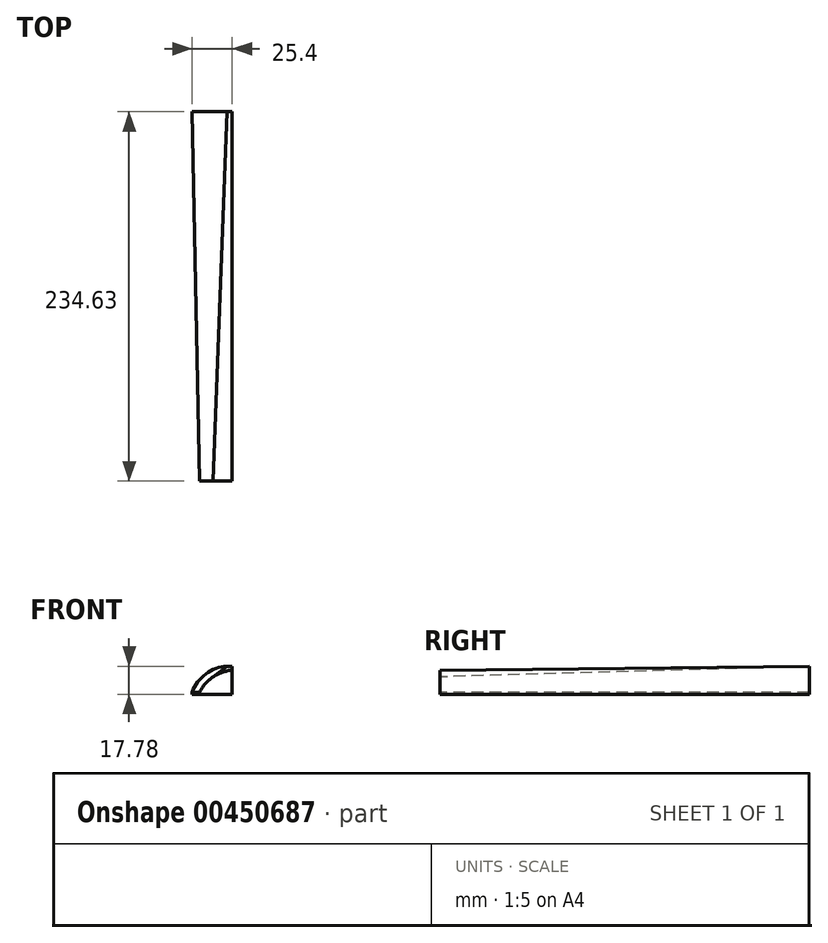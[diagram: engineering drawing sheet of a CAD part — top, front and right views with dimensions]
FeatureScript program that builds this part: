
annotation { "Feature Type Name" : "Feature", "Feature Type Description" : "" }
export const myFeature = defineFeature(function(context is Context, id is Id, definition is map)
    precondition{}
    {
        {
            var Q0;
            Q0=qCreatedBy(makeId("Front.planeOp"),FACE);
            var sketch = newSketch(context, id + "F0", { "sketchPlane" : qUnion([Q0])});
            skLineSegment(sketch, "E0", {"start": v(0, 0) * mm, "end": v(-20.64, 0) * mm});
            skLineSegment(sketch, "E1", {"start": v(0, 0) * mm, "end": v(0, 15.24) * mm});
            skLineSegment(sketch, "E2", {"start": v(-20.64, 0) * mm, "end": v(-20.64, 1.27) * mm});
            skArc(sketch, "E3", {"start": v(0, 15.24) * mm, "mid": v(-12.15, 10.96) * mm, "end": v(-20.64, 1.27) * mm});
            skSolve(sketch);
        }
        {
            var Q0;
            Q0=qCreatedBy(makeId("Right.planeOp"),FACE);
            var sketch = newSketch(context, id + "F1", { "sketchPlane" : qUnion([Q0])});
            skLineSegment(sketch, "E4", {"start": v(234.63, 0) * mm, "end": v(234.63, 17.78) * mm});
            skLineSegment(sketch, "E5", {"start": v(0, 15.24) * mm, "end": v(0, 0) * mm});
            skSolve(sketch);
        }
        {
            var Q0;
            Q0=sQuery(id+"F1.wireOp",EDGE,"E4");
            cPlane(context, id + "F2", {"entities" : qUnion([Q0]), "cplaneType" : CPlaneType.LINE_ANGLE, "offset" : 25.4 * mm, "angle" : 90 * degree, "oppositeDirection" : true, "width" : 152.4 * mm, "height" : 152.4 * mm});
        }
        {
            var Q0;
            Q0=qCreatedBy(id+"F2.planeOp",FACE);
            var sketch = newSketch(context, id + "F3", { "sketchPlane" : qUnion([Q0])});
            skLineSegment(sketch, "E6", {"start": v(0, 0) * mm, "end": v(-25.4, 0) * mm});
            skLineSegment(sketch, "E7", {"start": v(-25.4, 0) * mm, "end": v(-25.4, 1.27) * mm});
            skArc(sketch, "E8", {"start": v(-3.18, 17.78) * mm, "mid": v(-16.74, 12.82) * mm, "end": v(-25.4, 1.27) * mm});
            skLineSegment(sketch, "E9", {"start": v(0, 0) * mm, "end": v(0, 17.78) * mm});
            skLineSegment(sketch, "E10", {"start": v(0, 17.78) * mm, "end": v(-3.18, 17.78) * mm});
            skSolve(sketch);
        }
        {
            var Q0;
            Q0=makeQuery(id+"F3.imprint","IMPRINT",FACE,{"disambiguationData":[TD([[makeQuery(id+"F3.imprint","IMPRINT",EDGE,{"derivedFrom":sQuery(id+"F3.wireOp",EDGE,"E6")}),-1.0]])]});
            var Q1;
            Q1=makeQuery(id+"F0.imprint","IMPRINT",FACE,{"disambiguationData":[TD([[makeQuery(id+"F0.imprint","IMPRINT",EDGE,{"derivedFrom":sQuery(id+"F0.wireOp",EDGE,"E0")}),-1.0]])]});
            var Q2;
            Q2=sQuery(id+"F1.wireOp",EDGE,"Ofagh9u7-5ePs-uMly-TCfS-NPRzdzFGMTP7");
            var Q3;
            Q3=sQuery(id+"F1.wireOp",EDGE,"nO1nC4Vm-n3fs-rNI2-bCmv-2idzGEXgDerg");
            loft(context, id + "F4", {"addGuides" : true, "sheetProfilesArray" : [{ "sheetProfileEntities" : qUnion([Q0]) }, { "sheetProfileEntities" : qUnion([Q1]) }], "guidesArray" : [{ "guideEntities" : qUnion([Q2]), "guideDerivativeType" : LoftGuideDerivativeType.DEFAULT, "guideDerivativeMagnitude" : 1 }, { "guideEntities" : qUnion([Q3]), "guideDerivativeType" : LoftGuideDerivativeType.DEFAULT, "guideDerivativeMagnitude" : 1 }]});
        }
    });
